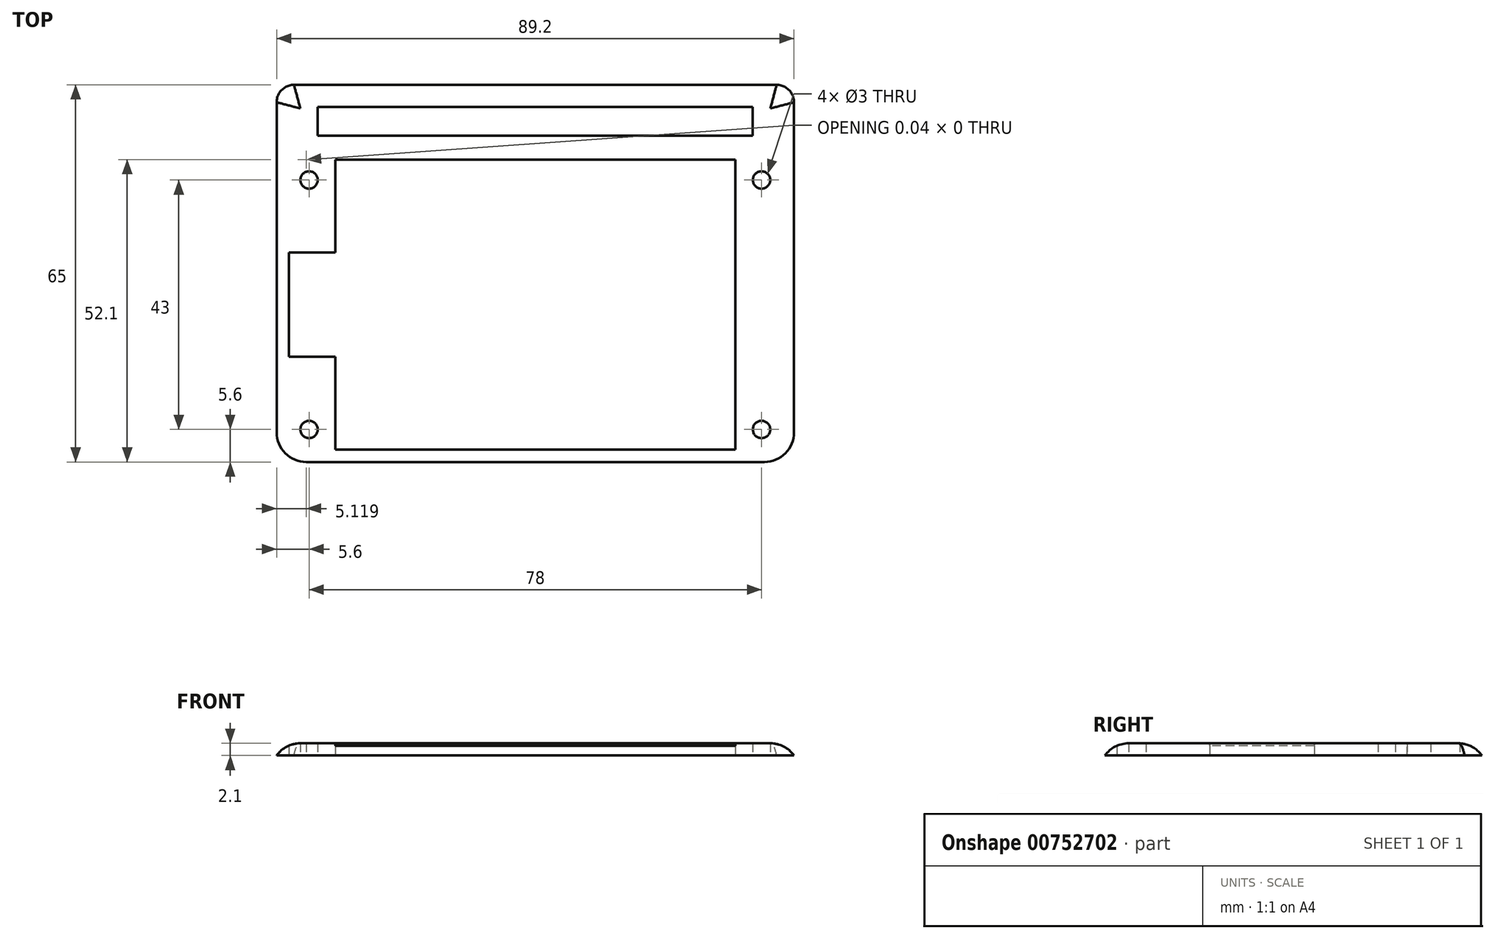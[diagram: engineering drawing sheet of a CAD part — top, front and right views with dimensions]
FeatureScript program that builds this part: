
annotation { "Feature Type Name" : "Feature", "Feature Type Description" : "" }
export const myFeature = defineFeature(function(context is Context, id is Id, definition is map)
    precondition{}
    {
        {
            var Q0;
            Q0=qCreatedBy(makeId("Top.planeOp"),FACE);
            var sketch = newSketch(context, id + "F0", { "sketchPlane" : qUnion([Q0])});
            skLineSegment(sketch, "E0.bottom", {"start": v(-39.5, 25) * mm, "end": v(39.5, 25) * mm});
            skLineSegment(sketch, "E0.top", {"start": v(-39.5, -25) * mm, "end": v(39.5, -25) * mm});
            skLineSegment(sketch, "E0.left", {"start": v(-42.5, 22) * mm, "end": v(-42.5, -22) * mm});
            skLineSegment(sketch, "E0.right", {"start": v(42.5, 22) * mm, "end": v(42.5, -22) * mm});
            skPoint(sketch, "E0.middle", {"position": v(0, 0) * mm});
            skLineSegment(sketch, "E1.bottom", {"start": v(-39, 21.5) * mm, "end": v(39, 21.5) * mm, "construction": true});
            skLineSegment(sketch, "E1.top", {"start": v(-39, -21.5) * mm, "end": v(39, -21.5) * mm, "construction": true});
            skLineSegment(sketch, "E1.left", {"start": v(-39, 21.5) * mm, "end": v(-39, -21.5) * mm, "construction": true});
            skLineSegment(sketch, "E1.right", {"start": v(39, 21.5) * mm, "end": v(39, -21.5) * mm, "construction": true});
            skCircle(sketch, "E2", {"center": v(-39, 21.5) * mm, "radius": 1.5 * mm});
            skCircle(sketch, "E3", {"center": v(39, 21.5) * mm, "radius": 1.5 * mm});
            skCircle(sketch, "E4", {"center": v(39, -21.5) * mm, "radius": 1.5 * mm});
            skCircle(sketch, "E5", {"center": v(-39, -21.5) * mm, "radius": 1.5 * mm});
            skPoint(sketch, "E6.visualSharp", {"position": v(-42.5, 25) * mm});
            skArc(sketch, "E6.filletArc", {"start": v(-39.5, 25) * mm, "mid": v(-41.62, 24.12) * mm, "end": v(-42.5, 22) * mm});
            skPoint(sketch, "E7.visualSharp", {"position": v(42.5, 25) * mm});
            skArc(sketch, "E7.filletArc", {"start": v(42.5, 22) * mm, "mid": v(41.62, 24.12) * mm, "end": v(39.5, 25) * mm});
            skPoint(sketch, "E8.visualSharp", {"position": v(42.5, -25) * mm});
            skArc(sketch, "E8.filletArc", {"start": v(39.5, -25) * mm, "mid": v(41.62, -24.12) * mm, "end": v(42.5, -22) * mm});
            skPoint(sketch, "E9.visualSharp", {"position": v(-42.5, -25) * mm});
            skArc(sketch, "E9.filletArc", {"start": v(-42.5, -22) * mm, "mid": v(-41.62, -24.12) * mm, "end": v(-39.5, -25) * mm});
            skLineSegment(sketch, "E10", {"start": v(0, 0) * mm, "end": v(-34.5, 0) * mm, "construction": true});
            skLineSegment(sketch, "E11", {"start": v(-34.5, 25) * mm, "end": v(-34.5, -25) * mm});
            skLineSegment(sketch, "E12", {"start": v(0, 0) * mm, "end": v(0, 9.32) * mm, "construction": true});
            skLineSegment(sketch, "E13.MirrorCS", {"start": v(34.5, 25) * mm, "end": v(34.5, -25) * mm});
            skLineSegment(sketch, "E14.1", {"start": v(-44.6, 22) * mm, "end": v(-44.6, -22) * mm});
            skLineSegment(sketch, "E14.2", {"start": v(-39.5, 27.1) * mm, "end": v(39.5, 27.1) * mm});
            skArc(sketch, "E14.3", {"start": v(-44.6, -22) * mm, "mid": v(-43.1, -25.6) * mm, "end": v(-39.5, -27.1) * mm});
            skLineSegment(sketch, "E14.5", {"start": v(44.6, 22) * mm, "end": v(44.6, -22) * mm});
            skArc(sketch, "E14.6", {"start": v(39.5, -27.1) * mm, "mid": v(43.1, -25.6) * mm, "end": v(44.6, -22) * mm});
            skLineSegment(sketch, "E14.7", {"start": v(-39.5, -27.1) * mm, "end": v(39.5, -27.1) * mm});
            skLineSegment(sketch, "E15", {"start": v(-42.5, 0) * mm, "end": v(-44.6, 0) * mm, "construction": true});
            skLineSegment(sketch, "E16.bottom", {"start": v(-44.6, 9) * mm, "end": v(-42.5, 9) * mm});
            skLineSegment(sketch, "E16.top", {"start": v(-44.6, -9) * mm, "end": v(-42.5, -9) * mm});
            skLineSegment(sketch, "E16.left", {"start": v(-44.6, 9) * mm, "end": v(-44.6, -9) * mm});
            skLineSegment(sketch, "E16.right", {"start": v(-42.5, 9) * mm, "end": v(-42.5, -9) * mm});
            skPoint(sketch, "E16.middle", {"position": v(-43.55, 0) * mm});
            skLineSegment(sketch, "E17", {"start": v(-42.5, 9) * mm, "end": v(-34.5, 9) * mm});
            skLineSegment(sketch, "E18", {"start": v(-42.5, -9) * mm, "end": v(-34.5, -9) * mm});
            skLineSegment(sketch, "E19", {"start": v(0, 27.1) * mm, "end": v(0, 36.1) * mm, "construction": true});
            skLineSegment(sketch, "E20", {"start": v(0, 36.1) * mm, "end": v(-39.5, 36.1) * mm});
            skLineSegment(sketch, "E21", {"start": v(0, 36.1) * mm, "end": v(39.5, 36.1) * mm});
            skLineSegment(sketch, "E22.0", {"start": v(0, 37.9) * mm, "end": v(41.6, 37.9) * mm});
            skLineSegment(sketch, "E22.1", {"start": v(0, 37.9) * mm, "end": v(-41.6, 37.9) * mm});
            skLineSegment(sketch, "E23", {"start": v(-42.5, 22) * mm, "end": v(-42.5, 33.1) * mm});
            skLineSegment(sketch, "E24", {"start": v(42.5, 22) * mm, "end": v(42.5, 33.1) * mm});
            skPoint(sketch, "E25.visualSharp", {"position": v(42.5, 36.1) * mm});
            skArc(sketch, "E25.filletArc", {"start": v(42.5, 33.1) * mm, "mid": v(41.62, 35.22) * mm, "end": v(39.5, 36.1) * mm});
            skPoint(sketch, "E26.visualSharp", {"position": v(-42.5, 36.1) * mm});
            skArc(sketch, "E26.filletArc", {"start": v(-39.5, 36.1) * mm, "mid": v(-41.62, 35.22) * mm, "end": v(-42.5, 33.1) * mm});
            skPoint(sketch, "E27.start.orphan", {"position": v(-44.6, 36.1) * mm});
            skPoint(sketch, "E28.start.orphan", {"position": v(44.6, 36.1) * mm});
            skLineSegment(sketch, "E29", {"start": v(-44.6, 22) * mm, "end": v(-44.6, 34.9) * mm});
            skLineSegment(sketch, "E30", {"start": v(44.6, 22) * mm, "end": v(44.6, 34.9) * mm});
            skPoint(sketch, "E31.visualSharp", {"position": v(-44.6, 37.9) * mm});
            skArc(sketch, "E31.filletArc", {"start": v(-41.6, 37.9) * mm, "mid": v(-43.72, 37.02) * mm, "end": v(-44.6, 34.9) * mm});
            skPoint(sketch, "E32.visualSharp", {"position": v(44.6, 37.9) * mm});
            skArc(sketch, "E32.filletArc", {"start": v(44.6, 34.9) * mm, "mid": v(43.72, 37.02) * mm, "end": v(41.6, 37.9) * mm});
            skLineSegment(sketch, "E33", {"start": v(-39.5, 27.1) * mm, "end": v(-42.5, 27.1) * mm});
            skLineSegment(sketch, "E34", {"start": v(39.5, 27.1) * mm, "end": v(42.5, 27.1) * mm});
            skEllipse(sketch, "E35", {"center": v(-39.42, 30.14) * mm, "majorRadius": 5.14 * mm, "minorRadius": 2.52 * mm, "majorAxis": v(-0.02, -1)});
            skLineSegment(sketch, "E36.bottom", {"start": v(-37.5, 29.1) * mm, "end": v(37.5, 29.1) * mm});
            skLineSegment(sketch, "E36.top", {"start": v(-37.5, 34.1) * mm, "end": v(37.5, 34.1) * mm});
            skLineSegment(sketch, "E36.left", {"start": v(-37.5, 29.1) * mm, "end": v(-37.5, 34.1) * mm});
            skLineSegment(sketch, "E36.right", {"start": v(37.5, 29.1) * mm, "end": v(37.5, 34.1) * mm});
            skPoint(sketch, "E36.middle", {"position": v(0, 31.6) * mm});
            skSolve(sketch);
        }
        {
            var Q0;
            Q0=makeQuery(id+"F0.imprint","IMPRINT",FACE,{"disambiguationData":[TD([[makeQuery(id+"F0.imprint","IMPRINT",EDGE,{"derivedFrom":sQuery(id+"F0.wireOp",EDGE,"E0.right")}),1.0]])]});
            var Q1;
            Q1=makeQuery(id+"F0.imprint","IMPRINT",FACE,{"disambiguationData":[TD([[makeQuery(id+"F0.imprint","IMPRINT",EDGE,{"derivedFrom":sQuery(id+"F0.wireOp",EDGE,"E2")}),-1.0]])]});
            var Q2;
            Q2=makeQuery(id+"F0.imprint","IMPRINT",FACE,{"disambiguationData":[TD([[makeQuery(id+"F0.imprint","IMPRINT",EDGE,{"derivedFrom":sQuery(id+"F0.wireOp",EDGE,"E5")}),-1.0]])]});
            var Q3;
            Q3=makeQuery(id+"F0.imprint","IMPRINT",FACE,{"disambiguationData":[TD([[makeQuery(id+"F0.imprint","IMPRINT",EDGE,{"derivedFrom":sQuery(id+"F0.wireOp",EDGE,"E0.right")}),-1.0]])]});
            var Q4;
            {var subQ0=sQuery(id+"F0.wireOp",EDGE,"E6.filletArc");Q4=makeQuery(id+"F0.imprint","IMPRINT",FACE,{"disambiguationData":[TD([[makeQuery(id+"F0.imprint","IMPRINT",EDGE,{"derivedFrom":subQ0}),-1.0]])]});}
            var Q5;
            Q5=makeQuery(id+"F0.imprint","IMPRINT",FACE,{"disambiguationData":[TD([[makeQuery(id+"F0.imprint","IMPRINT",EDGE,{"derivedFrom":sQuery(id+"F0.wireOp",EDGE,"E20")}),1.0]])]});
            var Q6;
            {var subQ0=sQuery(id+"F0.wireOp",EDGE,"E7.filletArc");Q6=makeQuery(id+"F0.imprint","IMPRINT",FACE,{"disambiguationData":[TD([[makeQuery(id+"F0.imprint","IMPRINT",EDGE,{"derivedFrom":subQ0}),-1.0]])]});}
            var Q7;
            {var subQ1=sQuery(id+"F0.wireOp",EDGE,"E33");var subQ5=sQuery(id+"F0.wireOp",EDGE,"E14.2");var subQ6=makeQuery(id+"F0.imprint","INTERSECT",VERTEX,{"derivedFrom":[subQ5,subQ1]});Q7=makeQuery(id+"F0.imprint","IMPRINT",FACE,{"disambiguationData":[TD([[makeQuery(id+"F0.imprint","IMPRINT",EDGE,{"disambiguationData":[TD([[subQ6,-1.0]])],"derivedFrom":subQ5}),1.0]])]});}
            var Q8;
            {var subQ3=sQuery(id+"F0.wireOp",EDGE,"E33");var subQ4=sQuery(id+"F0.wireOp",EDGE,"E14.2");var subQ5=makeQuery(id+"F0.imprint","INTERSECT",VERTEX,{"derivedFrom":[subQ4,subQ3]});Q8=makeQuery(id+"F0.imprint","IMPRINT",FACE,{"disambiguationData":[TD([[makeQuery(id+"F0.imprint","IMPRINT",EDGE,{"disambiguationData":[TD([[subQ5,-1.0]])],"derivedFrom":subQ4}),-1.0]])]});}
            var Q9;
            Q9=makeQuery(id+"F0.imprint","IMPRINT",FACE,{"disambiguationData":[TD([[makeQuery(id+"F0.imprint","IMPRINT",EDGE,{"derivedFrom":sQuery(id+"F0.wireOp",EDGE,"E16.right")}),1.0]])]});
            var Q10;
            Q10=makeQuery(id+"F0.imprint","IMPRINT",FACE,{"disambiguationData":[TD([[makeQuery(id+"F0.imprint","IMPRINT",EDGE,{"derivedFrom":sQuery(id+"F0.wireOp",EDGE,"E16.bottom")}),-1.0]])]});
            extrude(context, id + "F1", {"entities" : qUnion([Q0, Q1, Q2, Q3, Q4, Q5, Q6, Q7, Q8, Q9, Q10]), "depth" : 2.1 * mm, "offsetDistance" : 25 * mm});
        }
        {
            var Q0;
            Q0=makeQuery(id+"F1.opExtrude","CAP_EDGE",EDGE,{"disambiguationData":[OSD([sQuery(id+"F0.wireOp",EDGE,"E14.1"),sQuery(id+"F0.wireOp",EDGE,"E16.left"),sQuery(id+"F0.wireOp",EDGE,"E29")])],"isStart":false});
            fillet(context, id + "F2", {"entities" : qUnion([Q0]), "radius" : 5 * mm, "tangentPropagation" : true, "allowEdgeOverflow" : false});
        }
    });
